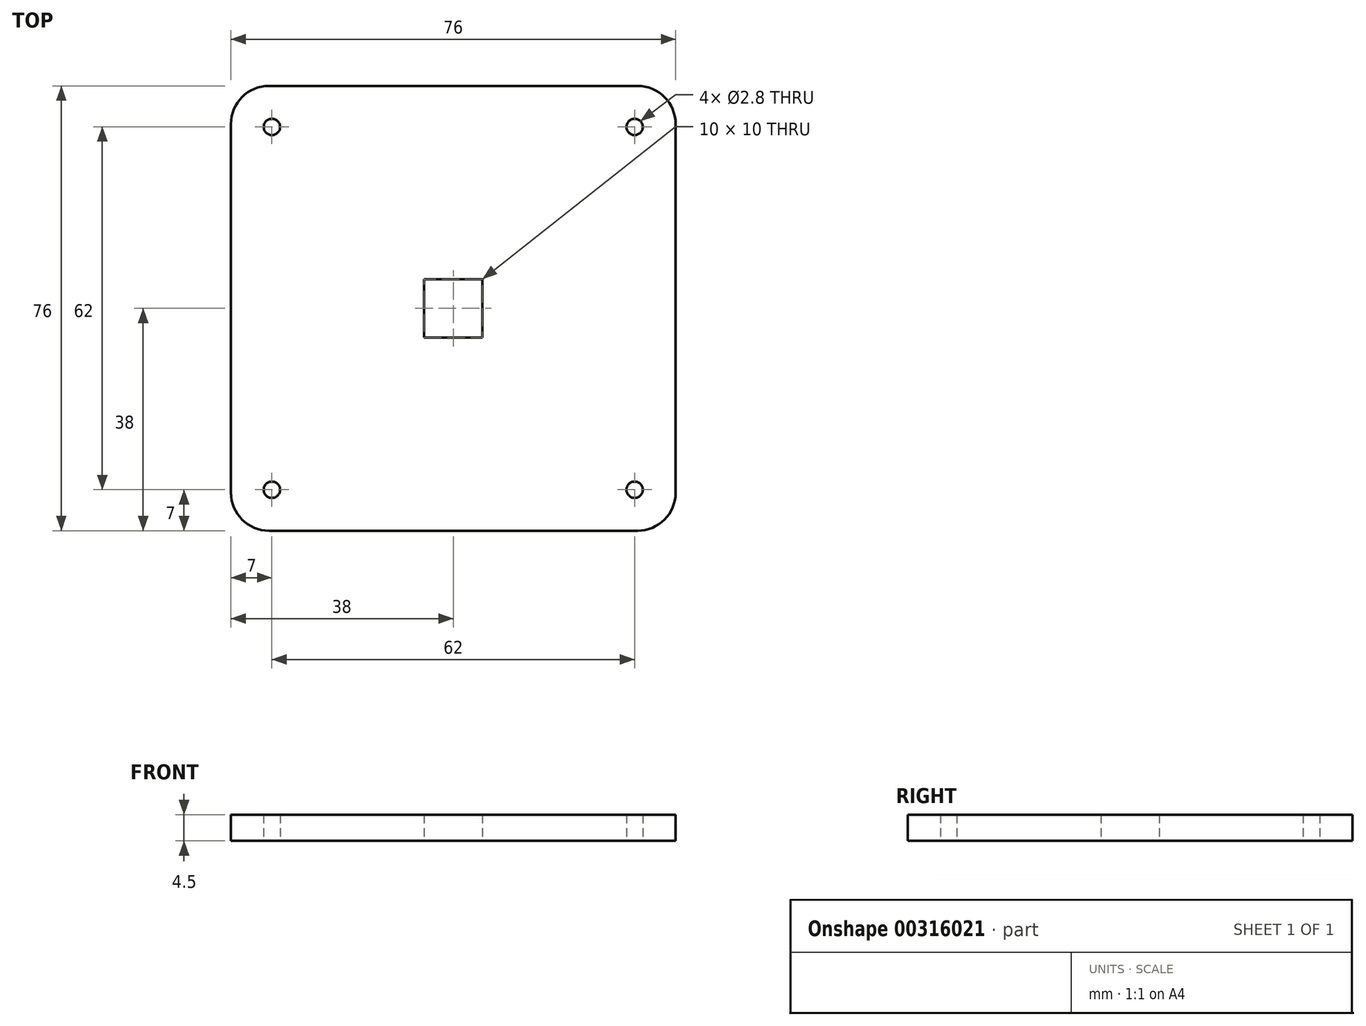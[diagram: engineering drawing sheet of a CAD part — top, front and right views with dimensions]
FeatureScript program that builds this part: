
annotation { "Feature Type Name" : "Feature", "Feature Type Description" : "" }
export const myFeature = defineFeature(function(context is Context, id is Id, definition is map)
    precondition{}
    {
        {
            var Q0;
            Q0=qCreatedBy(makeId("Top.planeOp"),FACE);
            var sketch = newSketch(context, id + "F0", { "sketchPlane" : qUnion([Q0])});
            skLineSegment(sketch, "E0.bottom", {"start": v(31.5, -38) * mm, "end": v(-31.5, -38) * mm});
            skLineSegment(sketch, "E0.top", {"start": v(31.5, 38) * mm, "end": v(-31.5, 38) * mm});
            skLineSegment(sketch, "E0.left", {"start": v(38, -31.5) * mm, "end": v(38, 31.5) * mm});
            skLineSegment(sketch, "E0.right", {"start": v(-38, -31.5) * mm, "end": v(-38, 31.5) * mm});
            skPoint(sketch, "E0.middle", {"position": v(0, 0) * mm});
            skLineSegment(sketch, "E1.bottom", {"start": v(5, -5) * mm, "end": v(-5, -5) * mm});
            skLineSegment(sketch, "E1.top", {"start": v(5, 5) * mm, "end": v(-5, 5) * mm});
            skLineSegment(sketch, "E1.left", {"start": v(5, -5) * mm, "end": v(5, 5) * mm});
            skLineSegment(sketch, "E1.right", {"start": v(-5, -5) * mm, "end": v(-5, 5) * mm});
            skPoint(sketch, "E2.visualSharp", {"position": v(-38, 38) * mm});
            skArc(sketch, "E2.filletArc", {"start": v(-31.5, 38) * mm, "mid": v(-36.1, 36.1) * mm, "end": v(-38, 31.5) * mm});
            skPoint(sketch, "E3.visualSharp", {"position": v(38, 38) * mm});
            skArc(sketch, "E3.filletArc", {"start": v(38, 31.5) * mm, "mid": v(36.1, 36.1) * mm, "end": v(31.5, 38) * mm});
            skPoint(sketch, "E4.visualSharp", {"position": v(38, -38) * mm});
            skArc(sketch, "E4.filletArc", {"start": v(31.5, -38) * mm, "mid": v(36.1, -36.1) * mm, "end": v(38, -31.5) * mm});
            skPoint(sketch, "E5.visualSharp", {"position": v(-38, -38) * mm});
            skArc(sketch, "E5.filletArc", {"start": v(-38, -31.5) * mm, "mid": v(-36.1, -36.1) * mm, "end": v(-31.5, -38) * mm});
            skLineSegment(sketch, "E6.bottom", {"start": v(31, -31) * mm, "end": v(-31, -31) * mm, "construction": true});
            skLineSegment(sketch, "E6.top", {"start": v(31, 31) * mm, "end": v(-31, 31) * mm, "construction": true});
            skLineSegment(sketch, "E6.left", {"start": v(31, -31) * mm, "end": v(31, 31) * mm, "construction": true});
            skLineSegment(sketch, "E6.right", {"start": v(-31, -31) * mm, "end": v(-31, 31) * mm, "construction": true});
            skCircle(sketch, "E7", {"center": v(-31, 31) * mm, "radius": 1.4 * mm});
            skCircle(sketch, "E8", {"center": v(31, 31) * mm, "radius": 1.4 * mm});
            skCircle(sketch, "E9", {"center": v(31, -31) * mm, "radius": 1.4 * mm});
            skCircle(sketch, "E10", {"center": v(-31, -31) * mm, "radius": 1.4 * mm});
            skSolve(sketch);
        }
        {
            var Q0;
            Q0=makeQuery(id+"F0.imprint","IMPRINT",FACE,{"disambiguationData":[TD([[makeQuery(id+"F0.imprint","IMPRINT",EDGE,{"derivedFrom":sQuery(id+"F0.wireOp",EDGE,"E0.bottom")}),-1.0]])]});
            extrude(context, id + "F1", {"entities" : qUnion([Q0]), "depth" : 4.5 * mm});
        }
    });
